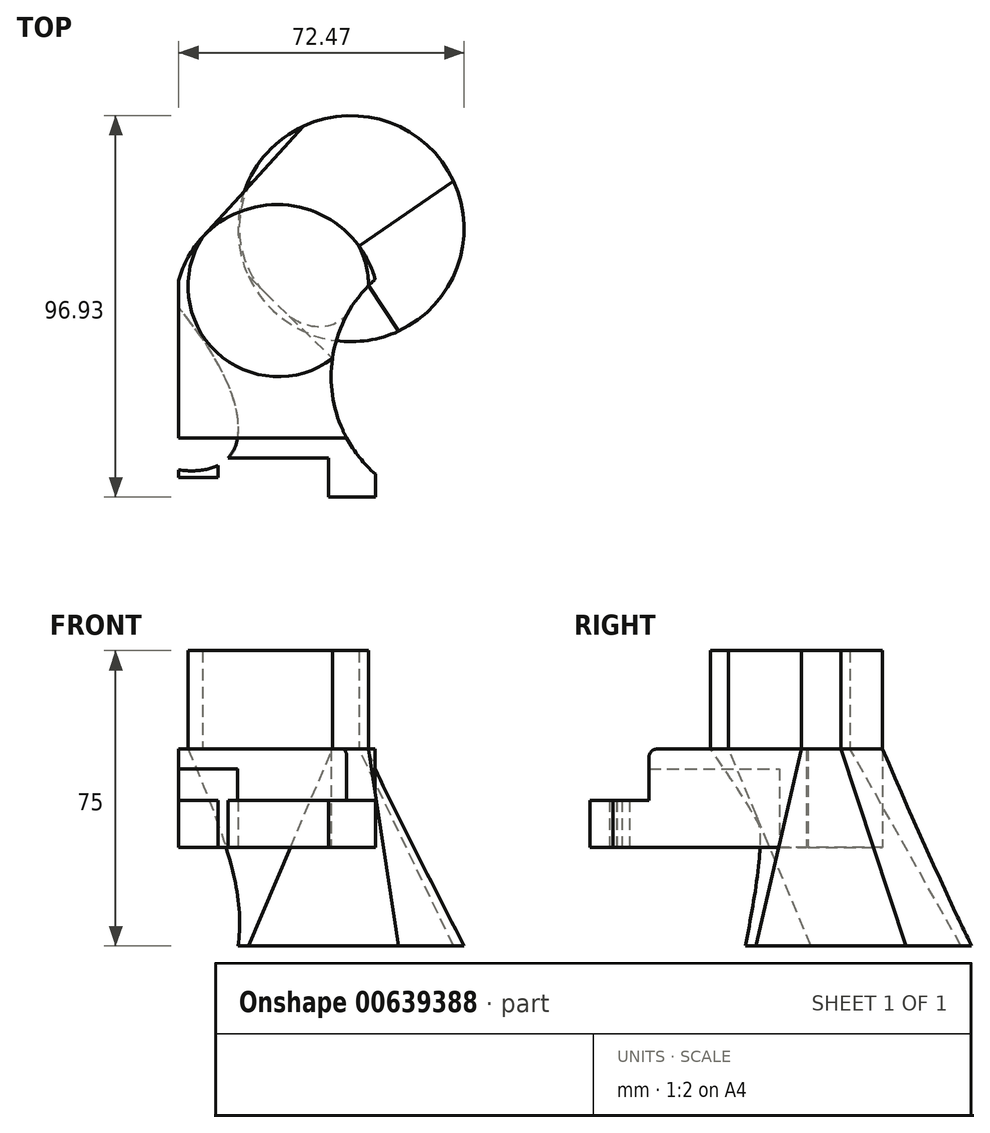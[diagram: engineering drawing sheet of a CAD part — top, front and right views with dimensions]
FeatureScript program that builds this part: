
annotation { "Feature Type Name" : "Feature", "Feature Type Description" : "" }
export const myFeature = defineFeature(function(context is Context, id is Id, definition is map)
    precondition{}
    {
        {
            var Q0;
            Q0=qCreatedBy(makeId("Top.planeOp"),FACE);
            var sketch = newSketch(context, id + "F0", { "sketchPlane" : qUnion([Q0])});
            skLineSegment(sketch, "E0.bottom", {"start": v(0, 0) * mm, "end": v(-50, 0) * mm});
            skLineSegment(sketch, "E0.top", {"start": v(0, 40) * mm, "end": v(-50, 40) * mm});
            skLineSegment(sketch, "E0.left", {"start": v(0, 0) * mm, "end": v(0, 40) * mm});
            skLineSegment(sketch, "E0.right", {"start": v(-50, 0) * mm, "end": v(-50, 40) * mm});
            skArc(sketch, "E1", {"start": v(0, 40) * mm, "mid": v(-25, 59.33) * mm, "end": v(-50, 40) * mm});
            skFitSpline(sketch, "E2", {"points": [v(-50, 40) * mm, v(-58.91, 27.11) * mm, v(-58.28, 18.41) * mm, v(-54, 9.71) * mm, v(-50, 0) * mm], "startDerivative": vector(-38.54, -44.23) * mm, "endDerivative": vector(15.3, -40.57) * mm});
            skSolve(sketch);
        }
        {
            var Q0;
            Q0=makeQuery(id+"F0.imprint","IMPRINT",FACE,{"disambiguationData":[TD([[makeQuery(id+"F0.imprint","IMPRINT",EDGE,{"derivedFrom":sQuery(id+"F0.wireOp",EDGE,"E0.top")}),-1.0]])]});
            var Q1;
            Q1=makeQuery(id+"F0.imprint","IMPRINT",FACE,{"disambiguationData":[TD([[makeQuery(id+"F0.imprint","IMPRINT",EDGE,{"derivedFrom":sQuery(id+"F0.wireOp",EDGE,"E0.bottom")}),-1.0]])]});
            extrude(context, id + "F1", {"entities" : qUnion([Q0, Q1]), "depth" : 25 * mm, "offsetDistance" : 25 * mm});
        }
        {
            var Q0;
            Q0=qCreatedBy(makeId("Top.planeOp"),FACE);
            var sketch = newSketch(context, id + "F2", { "sketchPlane" : qUnion([Q0])});
            skLineSegment(sketch, "E3", {"start": v(0, 0) * mm, "end": v(0, -15) * mm});
            skLineSegment(sketch, "E4", {"start": v(0, -15) * mm, "end": v(-12, -15) * mm});
            skLineSegment(sketch, "E5", {"start": v(-12, -15) * mm, "end": v(-12, -5) * mm});
            skLineSegment(sketch, "E6", {"start": v(-12, -5) * mm, "end": v(-40, -5) * mm});
            skLineSegment(sketch, "E7", {"start": v(-40, -5) * mm, "end": v(-40, -10) * mm});
            skLineSegment(sketch, "E8", {"start": v(-40, -10) * mm, "end": v(-50, -10) * mm});
            skLineSegment(sketch, "E9", {"start": v(-50, -10) * mm, "end": v(-50, 0) * mm});
            skLineSegment(sketch, "E10", {"start": v(0, 0) * mm, "end": v(-50, 0) * mm});
            skSolve(sketch);
        }
        {
            var Q0;
            Q0=makeQuery(id+"F1.opExtrude","CAP_EDGE",EDGE,{"disambiguationData":[OSD([sQuery(id+"F0.wireOp",EDGE,"E0.bottom")])],"isStart":false});
            fillet(context, id + "F3", {"entities" : qUnion([Q0]), "radius" : 2 * mm, "tangentPropagation" : true, "allowEdgeOverflow" : false});
        }
        {
            var Q0;
            Q0=makeQuery(id+"F2.imprint","IMPRINT",FACE,{"disambiguationData":[TD([[makeQuery(id+"F2.imprint","IMPRINT",EDGE,{"derivedFrom":sQuery(id+"F2.wireOp",EDGE,"E3")}),-1.0]])]});
            extrude(context, id + "F4", {"entities" : qUnion([Q0]), "operationType" : NewBodyOperationType.ADD, "depth" : 12 * mm, "offsetDistance" : 25 * mm});
        }
        {
            var Q0;
            Q0=qCreatedBy(makeId("Top.planeOp"),FACE);
            var sketch = newSketch(context, id + "F5", { "sketchPlane" : qUnion([Q0])});
            skCircle(sketch, "E11", {"center": v(21.63, 15.62) * mm, "radius": 32.9 * mm});
            skSolve(sketch);
        }
        {
            var Q0;
            Q0=makeQuery(id+"F5.imprint","IMPRINT",FACE,{"disambiguationData":[TD([[makeQuery(id+"F5.imprint","IMPRINT",EDGE,{"derivedFrom":sQuery(id+"F5.wireOp",EDGE,"E11")}),1.0]])]});
            extrude(context, id + "F6", {"entities" : qUnion([Q0]), "operationType" : NewBodyOperationType.REMOVE, "depth" : 30 * mm, "offsetDistance" : 25 * mm});
        }
        {
            var Q0;
            Q0=qCreatedBy(makeId("Top.planeOp"),FACE);
            var sketch = newSketch(context, id + "F7", { "sketchPlane" : qUnion([Q0])});
            skEllipse(sketch, "E12", {"center": v(-77.74, 30.76) * mm, "majorRadius": 53.9 * mm, "minorRadius": 21.52 * mm, "majorAxis": v(0.75, -0.66)});
            skSolve(sketch);
        }
        {
            var Q0;
            Q0=makeQuery(id+"F7.imprint","IMPRINT",FACE,{"disambiguationData":[TD([[makeQuery(id+"F7.imprint","IMPRINT",EDGE,{"derivedFrom":sQuery(id+"F7.wireOp",EDGE,"E12")}),1.0]])]});
            extrude(context, id + "F8", {"entities" : qUnion([Q0]), "operationType" : NewBodyOperationType.REMOVE, "depth" : 20 * mm, "offsetDistance" : 25 * mm});
        }
        {
            var Q0;
            Q0=makeQuery(id+"F1.opExtrude","CAP_FACE",FACE,{"disambiguationData":[OSD([sQuery(id+"F0.wireOp",EDGE,"E0.bottom"),sQuery(id+"F0.wireOp",EDGE,"E0.left"),sQuery(id+"F0.wireOp",EDGE,"E0.right"),sQuery(id+"F0.wireOp",EDGE,"E1")])],"isStart":false});
            var sketch = newSketch(context, id + "F9", { "sketchPlane" : qUnion([Q0])});
            skCircle(sketch, "E13", {"center": v(-24.7, 38.55) * mm, "radius": 22.93 * mm});
            skSolve(sketch);
        }
        {
            var Q0;
            Q0=qCreatedBy(makeId("Top.planeOp"),FACE);
            cPlane(context, id + "F10", {"entities" : qUnion([Q0]), "cplaneType" : CPlaneType.OFFSET, "offset" : 25 * mm, "oppositeDirection" : true, "width" : 150 * mm, "height" : 150 * mm});
        }
        {
            var Q0;
            Q0=qCreatedBy(id+"F10.planeOp",FACE);
            var sketch = newSketch(context, id + "F11", { "sketchPlane" : qUnion([Q0])});
            skCircle(sketch, "E14", {"center": v(-6.24, 53.22) * mm, "radius": 28.7 * mm});
            skSolve(sketch);
        }
        {
            var Q0;
            Q0=makeQuery(id+"F11.imprint","IMPRINT",FACE,{"disambiguationData":[TD([[makeQuery(id+"F11.imprint","IMPRINT",EDGE,{"derivedFrom":sQuery(id+"F11.wireOp",EDGE,"E14")}),1.0]])]});
            var Q1;
            {var subQ0=sQuery(id+"F9.wireOp",EDGE,"E13");var subQ1=sQuery(id+"F0.wireOp",EDGE,"E1");var subQ2=makeQuery(id+"F1.opExtrude","CAP_EDGE",EDGE,{"disambiguationData":[OSD([subQ1])],"isStart":false});var subQ3=makeQuery(id+"F9.imprint","INTERSECT",VERTEX,{"disambiguationData":[OD(0.0)],"derivedFrom":[subQ2,subQ0]});Q1=makeQuery(id+"F9.imprint","IMPRINT",FACE,{"disambiguationData":[TD([[makeQuery(id+"F9.imprint","IMPRINT",EDGE,{"disambiguationData":[TD([[subQ3,-1.0]])],"derivedFrom":subQ2}),1.0]])]});}
            loft(context, id + "F12", {"sheetProfilesArray" : [{ "sheetProfileEntities" : qUnion([Q0]) }, { "sheetProfileEntities" : qUnion([Q1]) }]});
        }
        {
            var Q0;
            {var subQ0=sQuery(id+"F9.wireOp",EDGE,"E13");var subQ1=sQuery(id+"F0.wireOp",EDGE,"E1");var subQ2=makeQuery(id+"F1.opExtrude","CAP_EDGE",EDGE,{"disambiguationData":[OSD([subQ1])],"isStart":false});var subQ3=makeQuery(id+"F9.imprint","INTERSECT",VERTEX,{"disambiguationData":[OD(0.0)],"derivedFrom":[subQ2,subQ0]});Q0=makeQuery(id+"F12.opLoft","CAP_FACE",FACE,{"disambiguationData":[OSD([makeQuery(id+"F9.imprint","IMPRINT",FACE,{"disambiguationData":[TD([[makeQuery(id+"F9.imprint","IMPRINT",EDGE,{"disambiguationData":[TD([[subQ3,-1.0]])],"derivedFrom":subQ2}),1.0]])]})])],"isStart":true});}
            extrude(context, id + "F13", {"entities" : qUnion([Q0]), "depth" : 25 * mm, "offsetDistance" : 25 * mm});
        }
    });
